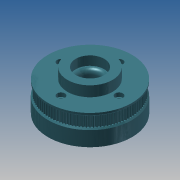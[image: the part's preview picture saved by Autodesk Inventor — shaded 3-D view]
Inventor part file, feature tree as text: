
AUTODESK INVENTOR PART (.ipt)
format: ipt  version: 2013 (Build 170138000, 138)  size: 1,297,408 bytes
history: native  units: mm
features: extrude x12, sketch x12, pattern_circular x2, chamfer x1, mirror x1, fillet x1
ambient origin geometry x8: Origin, YZ Plane, XZ Plane, XY Plane, X Axis, Y Axis, Z Axis, Center Point
bodies: Solid1 (feature_tree)
feature tree (29):
  extrude  "Extrusion1"  Depth=0.628319mm
  pattern_circular  "Circular Pattern1"  Count=100  [1 undecoded]
  extrude  "Extrusion3"  Depth=0.1mm
  chamfer  "Chamfer2"  Distance=2.5mm
  mirror  "Mirror1"
  extrude  "Extrusion7"  Depth=15.0mm
  extrude  "Extrusion8"  Depth=15.0mm
  extrude  "Extrusion9"  Depth=25.0mm
  extrude  "Extrusion10"  Depth=2.0mm TaperAngle=0.0deg
  extrude  "Extrusion11"  Depth=6.0mm
  pattern_circular  "Circular Pattern2"  [2 undecoded]
  extrude  "Extrusion12"  Depth=22.0mm
  fillet  "Fillet1"  Radius=7.0mm
  extrude  "Extrusion13"  Depth=1.0mm
  extrude  "Extrusion4"  Depth=35.0mm
  extrude  "Extrusion5"  Depth=8.0mm TaperAngle=0.0deg
  extrude  "Extrusion6"  Depth=15.0mm
  sketch  "Sketch1"  dims[d0=63.661977mm d9=0.628319mm]
  sketch  "Sketch3"  dims[d11=0.254mm]
  sketch  "Sketch4"  dims[d12=0.3mm]
  sketch  "Sketch5"  dims[d13=0.4mm]
  sketch  "Sketch6"  dims[d14=1.0mm]
  sketch  "Sketch7"  dims[d15=0.555mm]
  sketch  "Sketch8"  dims[d16=0.75mm]
  sketch  "Sketch9"  dims[d17=0.254mm]
  sketch  "Sketch10"  dims[d18=8.0mm d19=0.0mm d20=1000.0mm]
  sketch  "Sketch11"  dims[d21=360.0deg d23=0.1mm d32=2.5mm d33=0.0mm]
  sketch  "Sketch12"  dims[d34=1.0mm d35=2.0mm d36=45.0deg d37=15.0mm]
  sketch  "Sketch13"  dims[d39=3.5mm d40=15.0mm d41=25.0mm d42=2.0mm d43=0.0mm d44=6.0mm d46=3.0mm d47=0.0mm d49=22.0mm d51=7.0mm d52=0.0mm d53=1.0mm d54=35.0mm d56=8.0mm d57=0.0mm d58=15.0mm d60=10.0mm d61=0.0mm d62=22.0mm d64=7.0mm d65=0.0mm d68=22.5mm d69=3.5mm d70=7.0mm d71=0.0mm d72=6.0mm d74=3.0mm d75=0.0mm d76=40.0mm d77=360.0deg d80=10.0mm d81=0.0mm d82=3.5mm d83=65.0mm d85=10.0mm d86=0.0mm]
note: 3 required parameter values undecoded (feature->parameter linkage not recoverable at this tier; creation-order binding heuristic only, values carry confidence <= 0.55)
